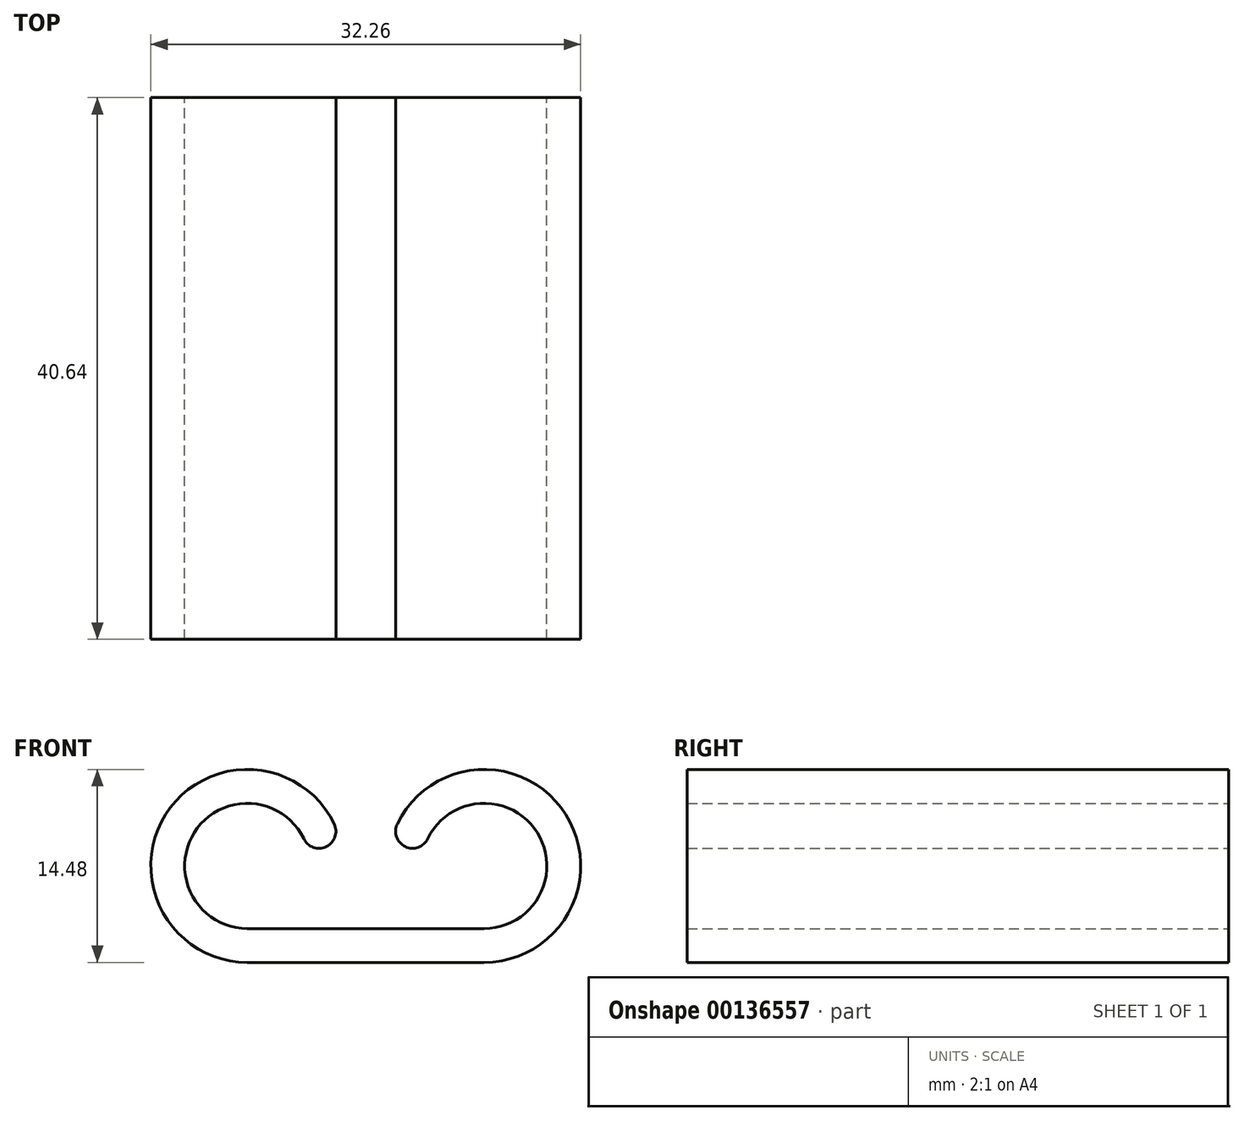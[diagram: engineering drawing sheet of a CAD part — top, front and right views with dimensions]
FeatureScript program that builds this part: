
annotation { "Feature Type Name" : "Feature", "Feature Type Description" : "" }
export const myFeature = defineFeature(function(context is Context, id is Id, definition is map)
    precondition{}
    {
        {
            var Q0;
            Q0=qCreatedBy(makeId("Front.planeOp"),FACE);
            var sketch = newSketch(context, id + "F0", { "sketchPlane" : qUnion([Q0])});
            skLineSegment(sketch, "E0", {"start": v(-8.89, 0) * mm, "end": v(0, 0) * mm});
            skArc(sketch, "E1", {"start": v(-4.66, 6.74) * mm, "mid": v(-12.87, 7.2) * mm, "end": v(-8.9, 0) * mm});
            skLineSegment(sketch, "E2.0", {"start": v(-8.89, -2.54) * mm, "end": v(0, -2.54) * mm});
            skArc(sketch, "E2.1", {"start": v(-2.37, 7.84) * mm, "mid": v(-15.02, 8.55) * mm, "end": v(-8.89, -2.54) * mm});
            skArc(sketch, "E3", {"start": v(-4.66, 6.74) * mm, "mid": v(-2.96, 6.15) * mm, "end": v(-2.37, 7.84) * mm});
            skLineSegment(sketch, "E4", {"start": v(0, 23.04) * mm, "end": v(0, -8.67) * mm, "construction": true});
            skArc(sketch, "E5.MirrorCS", {"start": v(4.66, 6.74) * mm, "mid": v(2.96, 6.15) * mm, "end": v(2.37, 7.84) * mm});
            skLineSegment(sketch, "E6.MirrorCS", {"start": v(8.9, -2.54) * mm, "end": v(0, -2.54) * mm});
            skArc(sketch, "E7.MirrorCS", {"start": v(4.66, 6.74) * mm, "mid": v(12.87, 7.2) * mm, "end": v(8.9, 0) * mm});
            skArc(sketch, "E8.MirrorCS", {"start": v(2.37, 7.84) * mm, "mid": v(15.02, 8.55) * mm, "end": v(8.9, -2.54) * mm});
            skLineSegment(sketch, "E9.MirrorCS", {"start": v(8.9, 0) * mm, "end": v(0, 0) * mm});
            skSolve(sketch);
        }
        {
            var Q0;
            Q0 = qSketchRegion(id + "F0", true);
            extrude(context, id + "F1", {"entities" : qUnion([Q0]), "endBound" : BoundingType.SYMMETRIC, "depth" : 40.64 * mm});
        }
    });
